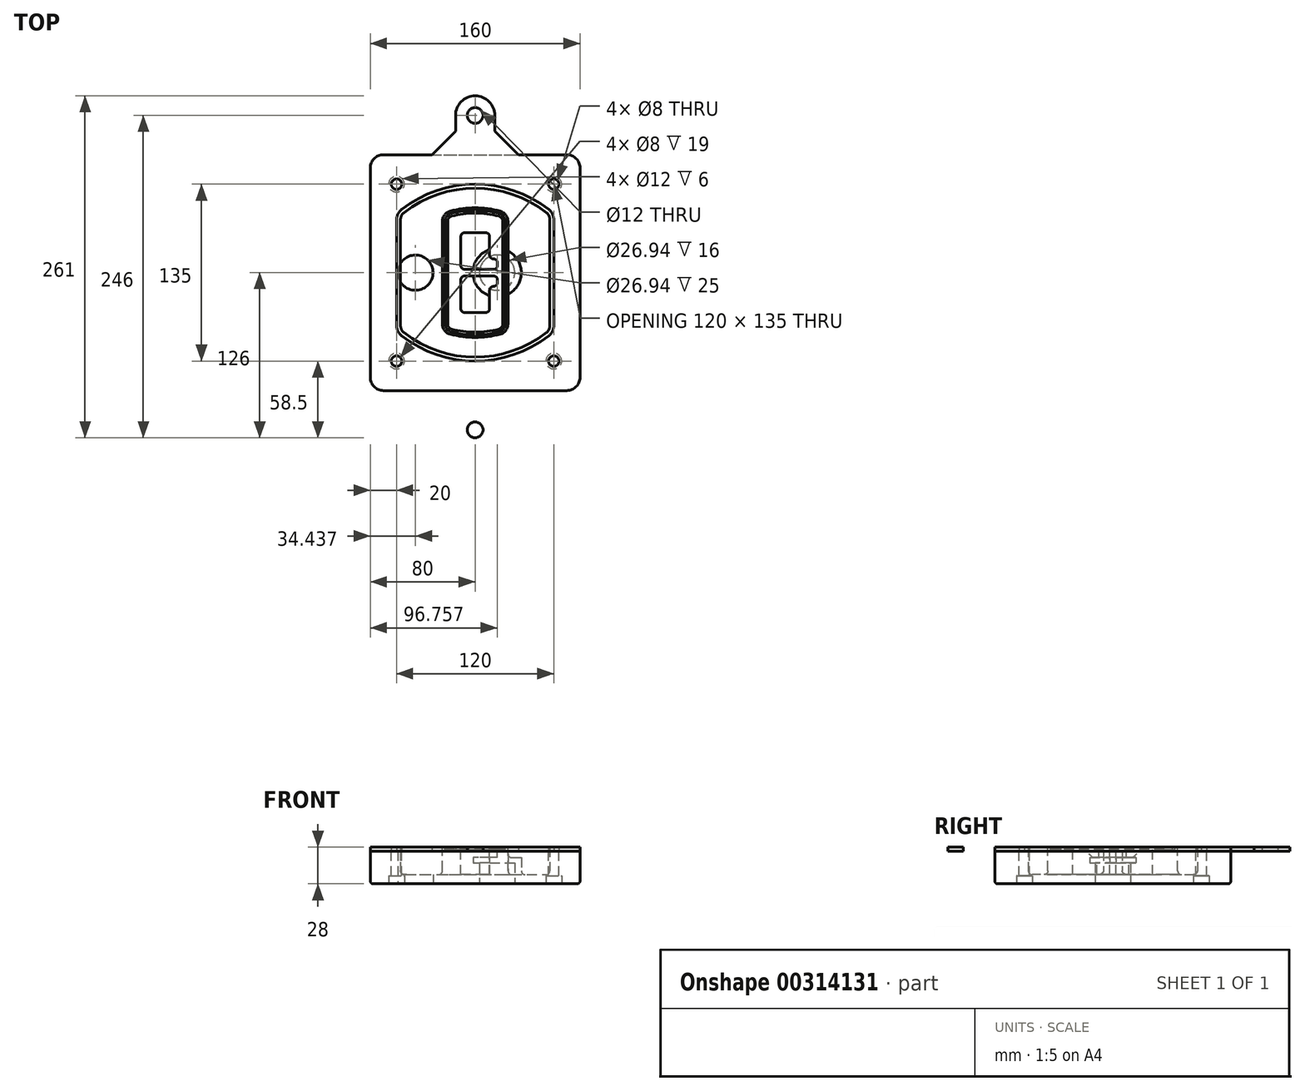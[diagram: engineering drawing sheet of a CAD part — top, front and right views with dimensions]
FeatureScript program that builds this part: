
annotation { "Feature Type Name" : "Feature", "Feature Type Description" : "" }
export const myFeature = defineFeature(function(context is Context, id is Id, definition is map)
    precondition{}
    {
        {
            var Q0;
            Q0=qCreatedBy(makeId("Top.planeOp"),FACE);
            var sketch = newSketch(context, id + "F0", { "sketchPlane" : qUnion([Q0])});
            skPoint(sketch, "E0.rect.middle", {"position": v(0, 0) * mm});
            skLineSegment(sketch, "E1.bottom", {"start": v(-70, -90) * mm, "end": v(70, -90) * mm});
            skLineSegment(sketch, "E1.top", {"start": v(-70, 90) * mm, "end": v(70, 90) * mm});
            skLineSegment(sketch, "E1.left", {"start": v(-80, -80) * mm, "end": v(-80, 80) * mm});
            skLineSegment(sketch, "E1.right", {"start": v(80, -80) * mm, "end": v(80, 80) * mm});
            skLineSegment(sketch, "E2", {"start": v(-80, 90) * mm, "end": v(80, -90) * mm, "construction": true});
            skLineSegment(sketch, "E3", {"start": v(80, 90) * mm, "end": v(-80, -90) * mm, "construction": true});
            skCircle(sketch, "E4", {"center": v(-60, 67.5) * mm, "radius": 4 * mm});
            skCircle(sketch, "E5", {"center": v(60, 67.5) * mm, "radius": 4 * mm});
            skCircle(sketch, "E6", {"center": v(60, -67.5) * mm, "radius": 4 * mm});
            skCircle(sketch, "E7", {"center": v(-60, -67.5) * mm, "radius": 4 * mm});
            skLineSegment(sketch, "E8", {"start": v(-60, 67.5) * mm, "end": v(60, 67.5) * mm, "construction": true});
            skLineSegment(sketch, "E9", {"start": v(60, 67.5) * mm, "end": v(60, -67.5) * mm, "construction": true});
            skLineSegment(sketch, "E10", {"start": v(60, -67.5) * mm, "end": v(-60, -67.5) * mm, "construction": true});
            skLineSegment(sketch, "E11", {"start": v(-60, -67.5) * mm, "end": v(-60, 67.5) * mm, "construction": true});
            skLineSegment(sketch, "E12", {"start": v(-60, 40.3) * mm, "end": v(-60, -40.3) * mm});
            skLineSegment(sketch, "E13", {"start": v(60, 40.3) * mm, "end": v(60, -40.3) * mm});
            skArc(sketch, "E14", {"start": v(56.15, 48.18) * mm, "mid": v(0, 67.5) * mm, "end": v(-56.15, 48.18) * mm});
            skArc(sketch, "E15", {"start": v(-56.15, -48.18) * mm, "mid": v(0, -67.5) * mm, "end": v(56.15, -48.18) * mm});
            skLineSegment(sketch, "E16", {"start": v(-60, 0) * mm, "end": v(60, 0) * mm, "construction": true});
            skPoint(sketch, "E17.visualSharp", {"position": v(-60, -45) * mm});
            skArc(sketch, "E17.filletArc", {"start": v(-60, -40.3) * mm, "mid": v(-58.99, -44.68) * mm, "end": v(-56.15, -48.18) * mm});
            skPoint(sketch, "E18.visualSharp", {"position": v(-60, 45) * mm});
            skArc(sketch, "E18.filletArc", {"start": v(-56.15, 48.18) * mm, "mid": v(-58.99, 44.68) * mm, "end": v(-60, 40.3) * mm});
            skPoint(sketch, "E19.visualSharp", {"position": v(60, 45) * mm});
            skArc(sketch, "E19.filletArc", {"start": v(60, 40.3) * mm, "mid": v(58.99, 44.68) * mm, "end": v(56.15, 48.18) * mm});
            skPoint(sketch, "E20.visualSharp", {"position": v(60, -45) * mm});
            skArc(sketch, "E20.filletArc", {"start": v(56.15, -48.18) * mm, "mid": v(58.99, -44.68) * mm, "end": v(60, -40.3) * mm});
            skPoint(sketch, "E21.visualSharp", {"position": v(-80, 90) * mm});
            skArc(sketch, "E21.filletArc", {"start": v(-70, 90) * mm, "mid": v(-77.07, 87.07) * mm, "end": v(-80, 80) * mm});
            skPoint(sketch, "E22.visualSharp", {"position": v(80, 90) * mm});
            skArc(sketch, "E22.filletArc", {"start": v(80, 80) * mm, "mid": v(77.07, 87.07) * mm, "end": v(70, 90) * mm});
            skPoint(sketch, "E23.visualSharp", {"position": v(80, -90) * mm});
            skArc(sketch, "E23.filletArc", {"start": v(70, -90) * mm, "mid": v(77.07, -87.07) * mm, "end": v(80, -80) * mm});
            skPoint(sketch, "E24.visualSharp", {"position": v(-80, -90) * mm});
            skArc(sketch, "E24.filletArc", {"start": v(-80, -80) * mm, "mid": v(-77.07, -87.07) * mm, "end": v(-70, -90) * mm});
            skArc(sketch, "E25.0", {"start": v(57, 40.3) * mm, "mid": v(56.3, 43.36) * mm, "end": v(54.3, 45.81) * mm});
            skLineSegment(sketch, "E25.1", {"start": v(57, 40.3) * mm, "end": v(57, -40.3) * mm});
            skArc(sketch, "E25.2", {"start": v(54.3, -45.81) * mm, "mid": v(56.3, -43.36) * mm, "end": v(57, -40.3) * mm});
            skArc(sketch, "E25.3", {"start": v(-54.3, -45.81) * mm, "mid": v(0, -64.5) * mm, "end": v(54.3, -45.81) * mm});
            skArc(sketch, "E25.4", {"start": v(-57, -40.3) * mm, "mid": v(-56.3, -43.36) * mm, "end": v(-54.3, -45.81) * mm});
            skArc(sketch, "E25.5", {"start": v(54.3, 45.81) * mm, "mid": v(0, 64.5) * mm, "end": v(-54.3, 45.81) * mm});
            skLineSegment(sketch, "E25.6", {"start": v(-57, 40.3) * mm, "end": v(-57, -40.3) * mm});
            skArc(sketch, "E25.7", {"start": v(-54.3, 45.81) * mm, "mid": v(-56.3, 43.36) * mm, "end": v(-57, 40.3) * mm});
            skArc(sketch, "E26.0", {"start": v(-58.62, 51.33) * mm, "mid": v(-62.58, 46.43) * mm, "end": v(-64, 40.3) * mm});
            skArc(sketch, "E26.1", {"start": v(58.62, 51.33) * mm, "mid": v(0, 71.5) * mm, "end": v(-58.62, 51.33) * mm});
            skArc(sketch, "E26.2", {"start": v(64, 40.3) * mm, "mid": v(62.58, 46.43) * mm, "end": v(58.62, 51.33) * mm});
            skLineSegment(sketch, "E26.3", {"start": v(64, 40.3) * mm, "end": v(64, -40.3) * mm});
            skArc(sketch, "E26.4", {"start": v(58.62, -51.33) * mm, "mid": v(62.58, -46.43) * mm, "end": v(64, -40.3) * mm});
            skLineSegment(sketch, "E26.5", {"start": v(-64, 40.3) * mm, "end": v(-64, -40.3) * mm});
            skArc(sketch, "E26.6", {"start": v(-58.62, -51.33) * mm, "mid": v(0, -71.5) * mm, "end": v(58.62, -51.33) * mm});
            skArc(sketch, "E26.7", {"start": v(-64, -40.3) * mm, "mid": v(-62.58, -46.43) * mm, "end": v(-58.62, -51.33) * mm});
            skSolve(sketch);
        }
        {
            var Q0;
            Q0=makeQuery(id+"F0.imprint","IMPRINT",FACE,{"disambiguationData":[TD([[makeQuery(id+"F0.imprint","IMPRINT",EDGE,{"derivedFrom":sQuery(id+"F0.wireOp",EDGE,"E1.bottom")}),1.0]])]});
            var Q1;
            Q1=makeQuery(id+"F0.imprint","IMPRINT",FACE,{"disambiguationData":[TD([[makeQuery(id+"F0.imprint","IMPRINT",EDGE,{"derivedFrom":sQuery(id+"F0.wireOp",EDGE,"E12")}),1.0]])]});
            var Q2;
            Q2=makeQuery(id+"F0.imprint","IMPRINT",FACE,{"disambiguationData":[TD([[makeQuery(id+"F0.imprint","IMPRINT",EDGE,{"derivedFrom":sQuery(id+"F0.wireOp",EDGE,"E25.0")}),1.0]])]});
            var Q3;
            Q3=makeQuery(id+"F0.imprint","IMPRINT",FACE,{"disambiguationData":[TD([[makeQuery(id+"F0.imprint","IMPRINT",EDGE,{"derivedFrom":sQuery(id+"F0.wireOp",EDGE,"E12")}),-1.0]])]});
            extrude(context, id + "F1", {"entities" : qUnion([Q0, Q1, Q2, Q3]), "oppositeDirection" : true, "depth" : 25 * mm});
        }
        {
            var Q0;
            Q0=makeQuery(id+"F0.imprint","IMPRINT",FACE,{"disambiguationData":[TD([[makeQuery(id+"F0.imprint","IMPRINT",EDGE,{"derivedFrom":sQuery(id+"F0.wireOp",EDGE,"E12")}),1.0]])]});
            extrude(context, id + "F2", {"entities" : qUnion([Q0]), "operationType" : NewBodyOperationType.ADD, "depth" : 3 * mm});
        }
        {
            var Q0;
            Q0=makeQuery(id+"F0.imprint","IMPRINT",FACE,{"disambiguationData":[TD([[makeQuery(id+"F0.imprint","IMPRINT",EDGE,{"derivedFrom":sQuery(id+"F0.wireOp",EDGE,"E25.0")}),1.0]])]});
            extrude(context, id + "F3", {"entities" : qUnion([Q0]), "operationType" : NewBodyOperationType.REMOVE, "oppositeDirection" : true, "depth" : 18 * mm});
        }
        {
            var Q0;
            Q0=makeQuery(id+"F2.opExtrude","CAP_FACE",FACE,{"disambiguationData":[OSD([sQuery(id+"F0.wireOp",EDGE,"E12"),sQuery(id+"F0.wireOp",EDGE,"E13"),sQuery(id+"F0.wireOp",EDGE,"E14"),sQuery(id+"F0.wireOp",EDGE,"E15"),sQuery(id+"F0.wireOp",EDGE,"E17.filletArc"),sQuery(id+"F0.wireOp",EDGE,"E18.filletArc"),sQuery(id+"F0.wireOp",EDGE,"E19.filletArc"),sQuery(id+"F0.wireOp",EDGE,"E20.filletArc"),sQuery(id+"F0.wireOp",EDGE,"E25.0"),sQuery(id+"F0.wireOp",EDGE,"E25.1"),sQuery(id+"F0.wireOp",EDGE,"E25.2"),sQuery(id+"F0.wireOp",EDGE,"E25.3"),sQuery(id+"F0.wireOp",EDGE,"E25.4"),sQuery(id+"F0.wireOp",EDGE,"E25.5"),sQuery(id+"F0.wireOp",EDGE,"E25.6"),sQuery(id+"F0.wireOp",EDGE,"E25.7")])],"isStart":false});
            var sketch = newSketch(context, id + "F4", { "sketchPlane" : qUnion([Q0])});
            skArc(sketch, "E27.0", {"start": v(-19.08, -46.97) * mm, "mid": v(0, -49.5) * mm, "end": v(19.08, -46.97) * mm});
            skArc(sketch, "E28.0", {"start": v(19.08, 46.97) * mm, "mid": v(0, 49.5) * mm, "end": v(-19.08, 46.97) * mm});
            skLineSegment(sketch, "E29", {"start": v(-25, 39.25) * mm, "end": v(-25, -39.25) * mm});
            skLineSegment(sketch, "E30", {"start": v(25, 39.25) * mm, "end": v(25, -39.25) * mm});
            skLineSegment(sketch, "E31", {"start": v(-25, 45.1) * mm, "end": v(25, 45.1) * mm, "construction": true});
            skLineSegment(sketch, "E32", {"start": v(-25, -45.1) * mm, "end": v(25, -45.1) * mm, "construction": true});
            skPoint(sketch, "E33.visualSharp", {"position": v(-25, 45.1) * mm});
            skArc(sketch, "E33.filletArc", {"start": v(-19.08, 46.97) * mm, "mid": v(-23.35, 44.11) * mm, "end": v(-25, 39.25) * mm});
            skPoint(sketch, "E34.visualSharp", {"position": v(25, 45.1) * mm});
            skArc(sketch, "E34.filletArc", {"start": v(25, 39.25) * mm, "mid": v(23.35, 44.11) * mm, "end": v(19.08, 46.97) * mm});
            skPoint(sketch, "E35.visualSharp", {"position": v(25, -45.1) * mm});
            skArc(sketch, "E35.filletArc", {"start": v(19.08, -46.97) * mm, "mid": v(23.35, -44.11) * mm, "end": v(25, -39.25) * mm});
            skPoint(sketch, "E36.visualSharp", {"position": v(-25, -45.1) * mm});
            skArc(sketch, "E36.filletArc", {"start": v(-25, -39.25) * mm, "mid": v(-23.35, -44.11) * mm, "end": v(-19.08, -46.97) * mm});
            skArc(sketch, "E37.0", {"start": v(54.3, 45.81) * mm, "mid": v(0, 64.5) * mm, "end": v(-54.3, 45.81) * mm});
            skArc(sketch, "E37.1", {"start": v(-54.3, 45.81) * mm, "mid": v(-56.3, 43.36) * mm, "end": v(-57, 40.3) * mm});
            skLineSegment(sketch, "E37.2", {"start": v(-57, 40.3) * mm, "end": v(-57, -40.3) * mm});
            skArc(sketch, "E37.3", {"start": v(-57, -40.3) * mm, "mid": v(-56.3, -43.36) * mm, "end": v(-54.3, -45.81) * mm});
            skArc(sketch, "E37.4", {"start": v(-54.3, -45.81) * mm, "mid": v(0, -64.5) * mm, "end": v(54.3, -45.81) * mm});
            skArc(sketch, "E37.5", {"start": v(54.3, -45.81) * mm, "mid": v(56.3, -43.36) * mm, "end": v(57, -40.3) * mm});
            skLineSegment(sketch, "E37.6", {"start": v(57, 40.3) * mm, "end": v(57, -40.3) * mm});
            skArc(sketch, "E37.7", {"start": v(57, 40.3) * mm, "mid": v(56.3, 43.36) * mm, "end": v(54.3, 45.81) * mm});
            skLineSegment(sketch, "E38.0", {"start": v(23, 39.25) * mm, "end": v(23, -39.25) * mm});
            skArc(sketch, "E38.1", {"start": v(18.56, -45.04) * mm, "mid": v(21.76, -42.9) * mm, "end": v(23, -39.25) * mm});
            skArc(sketch, "E38.2", {"start": v(-18.56, -45.04) * mm, "mid": v(0, -47.5) * mm, "end": v(18.56, -45.04) * mm});
            skArc(sketch, "E38.3", {"start": v(-23, -39.25) * mm, "mid": v(-21.76, -42.9) * mm, "end": v(-18.56, -45.04) * mm});
            skLineSegment(sketch, "E38.4", {"start": v(-23, 39.25) * mm, "end": v(-23, -39.25) * mm});
            skArc(sketch, "E38.5", {"start": v(23, 39.25) * mm, "mid": v(21.76, 42.9) * mm, "end": v(18.56, 45.04) * mm});
            skArc(sketch, "E38.6", {"start": v(-18.56, 45.04) * mm, "mid": v(-21.76, 42.9) * mm, "end": v(-23, 39.25) * mm});
            skArc(sketch, "E38.7", {"start": v(18.56, 45.04) * mm, "mid": v(0, 47.5) * mm, "end": v(-18.56, 45.04) * mm});
            skArc(sketch, "E39.0", {"start": v(21, 39.25) * mm, "mid": v(20.18, 41.68) * mm, "end": v(18.04, 43.1) * mm});
            skLineSegment(sketch, "E39.1", {"start": v(21, 39.25) * mm, "end": v(21, -39.25) * mm});
            skArc(sketch, "E39.2", {"start": v(18.04, -43.1) * mm, "mid": v(20.18, -41.68) * mm, "end": v(21, -39.25) * mm});
            skArc(sketch, "E39.3", {"start": v(-18.04, -43.1) * mm, "mid": v(0, -45.5) * mm, "end": v(18.04, -43.1) * mm});
            skArc(sketch, "E39.4", {"start": v(-21, -39.25) * mm, "mid": v(-20.18, -41.68) * mm, "end": v(-18.04, -43.1) * mm});
            skArc(sketch, "E39.5", {"start": v(18.04, 43.1) * mm, "mid": v(0, 45.5) * mm, "end": v(-18.04, 43.1) * mm});
            skLineSegment(sketch, "E39.6", {"start": v(-21, 39.25) * mm, "end": v(-21, -39.25) * mm});
            skArc(sketch, "E39.7", {"start": v(-18.04, 43.1) * mm, "mid": v(-20.18, 41.68) * mm, "end": v(-21, 39.25) * mm});
            skLineSegment(sketch, "E40", {"start": v(-25, 0) * mm, "end": v(25, 0) * mm, "construction": true});
            skLineSegment(sketch, "E41", {"start": v(-11, 5.5) * mm, "end": v(-11, 27.5) * mm});
            skLineSegment(sketch, "E42", {"start": v(-8, 30.5) * mm, "end": v(8, 30.5) * mm});
            skLineSegment(sketch, "E43", {"start": v(11, 27.5) * mm, "end": v(11, 13.5) * mm});
            skLineSegment(sketch, "E44", {"start": v(14, 10.5) * mm, "end": v(14, 10.5) * mm});
            skLineSegment(sketch, "E45", {"start": v(17, 7.5) * mm, "end": v(17, 5.5) * mm});
            skLineSegment(sketch, "E46", {"start": v(14, 2.5) * mm, "end": v(-8, 2.5) * mm});
            skPoint(sketch, "E47.visualSharp", {"position": v(-11, 30.5) * mm});
            skArc(sketch, "E47.filletArc", {"start": v(-8, 30.5) * mm, "mid": v(-10.12, 29.62) * mm, "end": v(-11, 27.5) * mm});
            skPoint(sketch, "E48.visualSharp", {"position": v(11, 30.5) * mm});
            skArc(sketch, "E48.filletArc", {"start": v(11, 27.5) * mm, "mid": v(10.12, 29.62) * mm, "end": v(8, 30.5) * mm});
            skPoint(sketch, "E49.visualSharp", {"position": v(11, 10.5) * mm});
            skArc(sketch, "E49.filletArc", {"start": v(11, 13.5) * mm, "mid": v(11.88, 11.38) * mm, "end": v(14, 10.5) * mm});
            skPoint(sketch, "E50.visualSharp", {"position": v(17, 10.5) * mm});
            skArc(sketch, "E50.filletArc", {"start": v(17, 7.5) * mm, "mid": v(16.12, 9.62) * mm, "end": v(14, 10.5) * mm});
            skPoint(sketch, "E51.visualSharp", {"position": v(17, 2.5) * mm});
            skArc(sketch, "E51.filletArc", {"start": v(14, 2.5) * mm, "mid": v(16.12, 3.38) * mm, "end": v(17, 5.5) * mm});
            skPoint(sketch, "E52.visualSharp", {"position": v(-11, 2.5) * mm});
            skArc(sketch, "E52.filletArc", {"start": v(-11, 5.5) * mm, "mid": v(-10.12, 3.38) * mm, "end": v(-8, 2.5) * mm});
            skLineSegment(sketch, "E53.0.MirrorCS", {"start": v(14, -2.5) * mm, "end": v(-8, -2.5) * mm});
            skArc(sketch, "E54.0.MirrorCS", {"start": v(-11, -5.5) * mm, "mid": v(-10.12, -3.38) * mm, "end": v(-8, -2.5) * mm});
            skLineSegment(sketch, "E55.0.MirrorCS", {"start": v(-11, -5.5) * mm, "end": v(-11, -27.5) * mm});
            skArc(sketch, "E56.0.MirrorCS", {"start": v(-8, -30.5) * mm, "mid": v(-10.12, -29.62) * mm, "end": v(-11, -27.5) * mm});
            skLineSegment(sketch, "E57.0.MirrorCS", {"start": v(-8, -30.5) * mm, "end": v(8, -30.5) * mm});
            skArc(sketch, "E58.0.MirrorCS", {"start": v(11, -27.5) * mm, "mid": v(10.12, -29.62) * mm, "end": v(8, -30.5) * mm});
            skLineSegment(sketch, "E59.0.MirrorCS", {"start": v(11, -27.5) * mm, "end": v(11, -13.5) * mm});
            skArc(sketch, "E60.0.MirrorCS", {"start": v(11, -13.5) * mm, "mid": v(11.88, -11.38) * mm, "end": v(14, -10.5) * mm});
            skArc(sketch, "E61.0.MirrorCS", {"start": v(17, -7.5) * mm, "mid": v(16.12, -9.62) * mm, "end": v(14, -10.5) * mm});
            skLineSegment(sketch, "E62.0.MirrorCS", {"start": v(17, -7.5) * mm, "end": v(17, -5.5) * mm});
            skArc(sketch, "E63.0.MirrorCS", {"start": v(14, -2.5) * mm, "mid": v(16.12, -3.38) * mm, "end": v(17, -5.5) * mm});
            skSolve(sketch);
        }
        {
            var Q0;
            Q0=makeQuery(id+"F4.imprint","IMPRINT",FACE,{"disambiguationData":[TD([[makeQuery(id+"F4.imprint","IMPRINT",EDGE,{"derivedFrom":sQuery(id+"F4.wireOp",EDGE,"E27.0")}),1.0]])]});
            var Q1;
            Q1=makeQuery(id+"F4.imprint","IMPRINT",FACE,{"disambiguationData":[TD([[makeQuery(id+"F4.imprint","IMPRINT",EDGE,{"derivedFrom":sQuery(id+"F4.wireOp",EDGE,"E38.0")}),-1.0]])]});
            var Q2;
            Q2=makeQuery(id+"F4.imprint","IMPRINT",FACE,{"disambiguationData":[TD([[makeQuery(id+"F4.imprint","IMPRINT",EDGE,{"derivedFrom":sQuery(id+"F4.wireOp",EDGE,"E39.0")}),1.0]])]});
            extrude(context, id + "F5", {"entities" : qUnion([Q0, Q1, Q2]), "operationType" : NewBodyOperationType.ADD, "endBound" : BoundingType.UP_TO_NEXT, "oppositeDirection" : true, "depth" : 25 * mm});
        }
        {
            var Q0;
            Q0=makeQuery(id+"F4.imprint","IMPRINT",FACE,{"disambiguationData":[TD([[makeQuery(id+"F4.imprint","IMPRINT",EDGE,{"derivedFrom":sQuery(id+"F4.wireOp",EDGE,"E38.0")}),-1.0]])]});
            extrude(context, id + "F6", {"entities" : qUnion([Q0]), "operationType" : NewBodyOperationType.REMOVE, "oppositeDirection" : true, "depth" : 2 * mm});
        }
        {
            var Q0;
            Q0=makeQuery(id+"F1.opExtrude","CAP_FACE",FACE,{"disambiguationData":[OSD([sQuery(id+"F0.wireOp",EDGE,"E1.bottom"),sQuery(id+"F0.wireOp",EDGE,"E1.top"),sQuery(id+"F0.wireOp",EDGE,"E1.left"),sQuery(id+"F0.wireOp",EDGE,"E1.right"),sQuery(id+"F0.wireOp",EDGE,"E4"),sQuery(id+"F0.wireOp",EDGE,"E5"),sQuery(id+"F0.wireOp",EDGE,"E6"),sQuery(id+"F0.wireOp",EDGE,"E7"),sQuery(id+"F0.wireOp",EDGE,"E21.filletArc"),sQuery(id+"F0.wireOp",EDGE,"E22.filletArc"),sQuery(id+"F0.wireOp",EDGE,"E23.filletArc"),sQuery(id+"F0.wireOp",EDGE,"E24.filletArc")])],"isStart":false});
            var sketch = newSketch(context, id + "F7", { "sketchPlane" : qUnion([Q0])});
            skCircle(sketch, "E64", {"center": v(16.76, 0) * mm, "radius": 13.47 * mm});
            skCircle(sketch, "E65", {"center": v(-45.56, 0) * mm, "radius": 13.47 * mm});
            skLineSegment(sketch, "E66", {"start": v(80, 0) * mm, "end": v(-80, 0) * mm});
            skCircle(sketch, "E67", {"center": v(16.76, 0) * mm, "radius": 18.47 * mm});
            skCircle(sketch, "E68", {"center": v(60, -67.5) * mm, "radius": 6 * mm});
            skCircle(sketch, "E69", {"center": v(-60, -67.5) * mm, "radius": 6 * mm});
            skCircle(sketch, "E70", {"center": v(-60, 67.5) * mm, "radius": 6 * mm});
            skCircle(sketch, "E71", {"center": v(60, 67.5) * mm, "radius": 6 * mm});
            skSolve(sketch);
        }
        {
            var Q0;
            {var subQ1=sQuery(id+"F7.wireOp",EDGE,"E66");var subQ4=sQuery(id+"F7.wireOp",EDGE,"E64");var subQ6=makeQuery(id+"F7.imprint","INTERSECT",VERTEX,{"disambiguationData":[OD(0.0)],"derivedFrom":[subQ4,subQ1]});Q0=makeQuery(id+"F7.imprint","IMPRINT",FACE,{"disambiguationData":[TD([[makeQuery(id+"F7.imprint","IMPRINT",EDGE,{"disambiguationData":[TD([[subQ6,-1.0]])],"derivedFrom":subQ4}),-1.0]])]});}
            var Q1;
            {var subQ0=sQuery(id+"F7.wireOp",EDGE,"E66");var subQ1=sQuery(id+"F7.wireOp",EDGE,"E64");var subQ3=makeQuery(id+"F7.imprint","INTERSECT",VERTEX,{"disambiguationData":[OD(0.0)],"derivedFrom":[subQ1,subQ0]});Q1=makeQuery(id+"F7.imprint","IMPRINT",FACE,{"disambiguationData":[TD([[makeQuery(id+"F7.imprint","IMPRINT",EDGE,{"disambiguationData":[TD([[subQ3,-1.0]])],"derivedFrom":subQ1}),1.0]])]});}
            var Q2;
            {var subQ0=sQuery(id+"F7.wireOp",EDGE,"E66");var subQ1=sQuery(id+"F7.wireOp",EDGE,"E64");var subQ3=makeQuery(id+"F7.imprint","INTERSECT",VERTEX,{"disambiguationData":[OD(0.0)],"derivedFrom":[subQ1,subQ0]});Q2=makeQuery(id+"F7.imprint","IMPRINT",FACE,{"disambiguationData":[TD([[makeQuery(id+"F7.imprint","IMPRINT",EDGE,{"disambiguationData":[TD([[subQ3,1.0]])],"derivedFrom":subQ1}),1.0]])]});}
            var Q3;
            {var subQ1=sQuery(id+"F7.wireOp",EDGE,"E66");var subQ4=sQuery(id+"F7.wireOp",EDGE,"E64");var subQ6=makeQuery(id+"F7.imprint","INTERSECT",VERTEX,{"disambiguationData":[OD(0.0)],"derivedFrom":[subQ4,subQ1]});Q3=makeQuery(id+"F7.imprint","IMPRINT",FACE,{"disambiguationData":[TD([[makeQuery(id+"F7.imprint","IMPRINT",EDGE,{"disambiguationData":[TD([[subQ6,1.0]])],"derivedFrom":subQ4}),-1.0]])]});}
            extrude(context, id + "F8", {"entities" : qUnion([Q0, Q1, Q2, Q3]), "operationType" : NewBodyOperationType.ADD, "oppositeDirection" : true, "depth" : 20 * mm});
        }
        {
            var Q0;
            {var subQ0=sQuery(id+"F7.wireOp",EDGE,"E66");var subQ1=sQuery(id+"F7.wireOp",EDGE,"E64");var subQ3=makeQuery(id+"F7.imprint","INTERSECT",VERTEX,{"disambiguationData":[OD(0.0)],"derivedFrom":[subQ1,subQ0]});Q0=makeQuery(id+"F7.imprint","IMPRINT",FACE,{"disambiguationData":[TD([[makeQuery(id+"F7.imprint","IMPRINT",EDGE,{"disambiguationData":[TD([[subQ3,-1.0]])],"derivedFrom":subQ1}),1.0]])]});}
            var Q1;
            {var subQ0=sQuery(id+"F7.wireOp",EDGE,"E66");var subQ1=sQuery(id+"F7.wireOp",EDGE,"E64");var subQ3=makeQuery(id+"F7.imprint","INTERSECT",VERTEX,{"disambiguationData":[OD(0.0)],"derivedFrom":[subQ1,subQ0]});Q1=makeQuery(id+"F7.imprint","IMPRINT",FACE,{"disambiguationData":[TD([[makeQuery(id+"F7.imprint","IMPRINT",EDGE,{"disambiguationData":[TD([[subQ3,1.0]])],"derivedFrom":subQ1}),1.0]])]});}
            extrude(context, id + "F9", {"entities" : qUnion([Q0, Q1]), "operationType" : NewBodyOperationType.REMOVE, "oppositeDirection" : true, "depth" : 16 * mm});
        }
        {
            var Q0;
            {var subQ0=sQuery(id+"F7.wireOp",EDGE,"E66");var subQ1=sQuery(id+"F7.wireOp",EDGE,"E65");var subQ3=makeQuery(id+"F7.imprint","INTERSECT",VERTEX,{"disambiguationData":[OD(0.0)],"derivedFrom":[subQ1,subQ0]});Q0=makeQuery(id+"F7.imprint","IMPRINT",FACE,{"disambiguationData":[TD([[makeQuery(id+"F7.imprint","IMPRINT",EDGE,{"disambiguationData":[TD([[subQ3,-1.0]])],"derivedFrom":subQ1}),1.0]])]});}
            var Q1;
            {var subQ0=sQuery(id+"F7.wireOp",EDGE,"E66");var subQ1=sQuery(id+"F7.wireOp",EDGE,"E65");var subQ3=makeQuery(id+"F7.imprint","INTERSECT",VERTEX,{"disambiguationData":[OD(0.0)],"derivedFrom":[subQ1,subQ0]});Q1=makeQuery(id+"F7.imprint","IMPRINT",FACE,{"disambiguationData":[TD([[makeQuery(id+"F7.imprint","IMPRINT",EDGE,{"disambiguationData":[TD([[subQ3,1.0]])],"derivedFrom":subQ1}),1.0]])]});}
            extrude(context, id + "F10", {"entities" : qUnion([Q0, Q1]), "operationType" : NewBodyOperationType.REMOVE, "oppositeDirection" : true, "depth" : 25 * mm});
        }
        {
            var Q0;
            Q0=makeQuery(id+"F7.imprint","IMPRINT",FACE,{"disambiguationData":[TD([[makeQuery(id+"F7.imprint","IMPRINT",EDGE,{"derivedFrom":sQuery(id+"F7.wireOp",EDGE,"E68")}),1.0]])]});
            var Q1;
            Q1=makeQuery(id+"F7.imprint","IMPRINT",FACE,{"disambiguationData":[TD([[makeQuery(id+"F7.imprint","IMPRINT",EDGE,{"derivedFrom":makeQuery(id+"F1.opExtrude","CAP_EDGE",EDGE,{"disambiguationData":[OSD([sQuery(id+"F0.wireOp",EDGE,"E5")])],"isStart":false})}),-1.0]])]});
            var Q2;
            Q2=makeQuery(id+"F7.imprint","IMPRINT",FACE,{"disambiguationData":[TD([[makeQuery(id+"F7.imprint","IMPRINT",EDGE,{"derivedFrom":sQuery(id+"F7.wireOp",EDGE,"E69")}),1.0]])]});
            var Q3;
            Q3=makeQuery(id+"F7.imprint","IMPRINT",FACE,{"disambiguationData":[TD([[makeQuery(id+"F7.imprint","IMPRINT",EDGE,{"derivedFrom":makeQuery(id+"F1.opExtrude","CAP_EDGE",EDGE,{"disambiguationData":[OSD([sQuery(id+"F0.wireOp",EDGE,"E4")])],"isStart":false})}),-1.0]])]});
            var Q4;
            Q4=makeQuery(id+"F7.imprint","IMPRINT",FACE,{"disambiguationData":[TD([[makeQuery(id+"F7.imprint","IMPRINT",EDGE,{"derivedFrom":sQuery(id+"F7.wireOp",EDGE,"E70")}),1.0]])]});
            var Q5;
            Q5=makeQuery(id+"F7.imprint","IMPRINT",FACE,{"disambiguationData":[TD([[makeQuery(id+"F7.imprint","IMPRINT",EDGE,{"derivedFrom":makeQuery(id+"F1.opExtrude","CAP_EDGE",EDGE,{"disambiguationData":[OSD([sQuery(id+"F0.wireOp",EDGE,"E7")])],"isStart":false})}),-1.0]])]});
            var Q6;
            Q6=makeQuery(id+"F7.imprint","IMPRINT",FACE,{"disambiguationData":[TD([[makeQuery(id+"F7.imprint","IMPRINT",EDGE,{"derivedFrom":sQuery(id+"F7.wireOp",EDGE,"E71")}),1.0]])]});
            var Q7;
            Q7=makeQuery(id+"F7.imprint","IMPRINT",FACE,{"disambiguationData":[TD([[makeQuery(id+"F7.imprint","IMPRINT",EDGE,{"derivedFrom":makeQuery(id+"F1.opExtrude","CAP_EDGE",EDGE,{"disambiguationData":[OSD([sQuery(id+"F0.wireOp",EDGE,"E6")])],"isStart":false})}),-1.0]])]});
            extrude(context, id + "F11", {"entities" : qUnion([Q0, Q1, Q2, Q3, Q4, Q5, Q6, Q7]), "operationType" : NewBodyOperationType.REMOVE, "oppositeDirection" : true, "depth" : 6 * mm});
        }
        {
            var Q0;
            Q0=makeQuery(id+"F9.boolean.opBoolean","COPY",FACE,{"derivedFrom":makeQuery(id+"F9.opExtrude","CAP_FACE",FACE,{"disambiguationData":[OSD([sQuery(id+"F7.wireOp",EDGE,"E64")])],"isStart":false})});
            var sketch = newSketch(context, id + "F12", { "sketchPlane" : qUnion([Q0])});
            skArc(sketch, "E72.0", {"start": v(11, 17.55) * mm, "mid": v(2.57, 11.82) * mm, "end": v(-1.54, 2.5) * mm});
            skArc(sketch, "E72.1", {"start": v(-1.54, -2.5) * mm, "mid": v(2.57, -11.82) * mm, "end": v(11, -17.55) * mm});
            skLineSegment(sketch, "E73", {"start": v(-1.54, -2.5) * mm, "end": v(14, -2.5) * mm});
            skLineSegment(sketch, "E74.0", {"start": v(14, 2.5) * mm, "end": v(-1.54, 2.5) * mm});
            skArc(sketch, "E74.1", {"start": v(14, 2.5) * mm, "mid": v(16.12, 3.38) * mm, "end": v(17, 5.5) * mm});
            skLineSegment(sketch, "E74.2", {"start": v(17, 7.5) * mm, "end": v(17, 5.5) * mm});
            skArc(sketch, "E74.3", {"start": v(17, 7.5) * mm, "mid": v(16.12, 9.62) * mm, "end": v(14, 10.5) * mm});
            skArc(sketch, "E74.4", {"start": v(11, 13.5) * mm, "mid": v(11.88, 11.38) * mm, "end": v(14, 10.5) * mm});
            skLineSegment(sketch, "E74.5", {"start": v(11, 17.55) * mm, "end": v(11, 13.5) * mm});
            skLineSegment(sketch, "E74.7", {"start": v(14, -2.5) * mm, "end": v(-1.54, -2.5) * mm});
            skArc(sketch, "E74.8", {"start": v(14, -2.5) * mm, "mid": v(16.12, -3.38) * mm, "end": v(17, -5.5) * mm});
            skLineSegment(sketch, "E74.9", {"start": v(17, -7.5) * mm, "end": v(17, -5.5) * mm});
            skArc(sketch, "E74.10", {"start": v(17, -7.5) * mm, "mid": v(16.12, -9.62) * mm, "end": v(14, -10.5) * mm});
            skArc(sketch, "E74.11", {"start": v(11, -13.5) * mm, "mid": v(11.88, -11.38) * mm, "end": v(14, -10.5) * mm});
            skLineSegment(sketch, "E74.12", {"start": v(11, -17.55) * mm, "end": v(11, -13.5) * mm});
            skPoint(sketch, "E75.orphan", {"position": v(11, -27.5) * mm});
            skPoint(sketch, "E76.orphan", {"position": v(-8, -2.5) * mm});
            skPoint(sketch, "E77.orphan", {"position": v(-8, 2.5) * mm});
            skPoint(sketch, "E78.orphan", {"position": v(11, 27.5) * mm});
            skSolve(sketch);
        }
        {
            var Q0;
            {var subQ7=sQuery(id+"F12.wireOp",EDGE,"E72.0");var subQ14=sQuery(id+"F12.wireOp",EDGE,"E72.1");var subQ16=sQuery(id+"F12.wireOp",EDGE,"E74.1");var subQ18=sQuery(id+"F12.wireOp",EDGE,"E74.8");Q0=qUnion([makeQuery(id+"F12.imprint","IMPRINT",FACE,{"disambiguationData":[TD([[makeQuery(id+"F12.imprint","IMPRINT",EDGE,{"derivedFrom":subQ7}),1.0]])]}),makeQuery(id+"F12.imprint","IMPRINT",FACE,{"disambiguationData":[TD([[makeQuery(id+"F12.imprint","IMPRINT",EDGE,{"derivedFrom":subQ14}),1.0]])]}),makeQuery(id+"F12.imprint","IMPRINT",FACE,{"disambiguationData":[TD([[makeQuery(id+"F12.imprint","IMPRINT",EDGE,{"derivedFrom":subQ16}),1.0]])]}),makeQuery(id+"F12.imprint","IMPRINT",FACE,{"disambiguationData":[TD([[makeQuery(id+"F12.imprint","IMPRINT",EDGE,{"derivedFrom":subQ18}),-1.0]])]})]);}
            var Q1;
            Q1=makeQuery(id+"F5.boolean.opBoolean","SPLIT",FACE,{"disambiguationData":[TD([makeQuery(id+"F5.opExtrude","SWEPT_FACE",FACE,{"disambiguationData":[OSD([sQuery(id+"F4.wireOp",EDGE,"E41")])]})])],"derivedFrom":makeQuery(id+"F3.boolean.opBoolean","COPY",FACE,{"derivedFrom":makeQuery(id+"F3.opExtrude","CAP_FACE",FACE,{"disambiguationData":[OSD([sQuery(id+"F0.wireOp",EDGE,"E25.0"),sQuery(id+"F0.wireOp",EDGE,"E25.1"),sQuery(id+"F0.wireOp",EDGE,"E25.2"),sQuery(id+"F0.wireOp",EDGE,"E25.3"),sQuery(id+"F0.wireOp",EDGE,"E25.4"),sQuery(id+"F0.wireOp",EDGE,"E25.5"),sQuery(id+"F0.wireOp",EDGE,"E25.6"),sQuery(id+"F0.wireOp",EDGE,"E25.7")])],"isStart":false})})});
            extrude(context, id + "F13", {"entities" : qUnion([Q0]), "operationType" : NewBodyOperationType.REMOVE, "endBound" : BoundingType.UP_TO_SURFACE, "endBoundEntityFace" : qUnion([Q1]), "depth" : 25 * mm});
        }
        {
            var Q0;
            Q0=makeQuery(id+"F3.boolean.opBoolean","COPY",EDGE,{"derivedFrom":makeQuery(id+"F3.opExtrude","CAP_EDGE",EDGE,{"disambiguationData":[OSD([sQuery(id+"F0.wireOp",EDGE,"E25.6")])],"isStart":false})});
            var Q1;
            Q1=makeQuery(id+"F8.boolean.opBoolean","INTERSECT",EDGE,{"derivedFrom":[makeQuery(id+"F5.opExtrude","SWEPT_FACE",FACE,{"disambiguationData":[OSD([sQuery(id+"F4.wireOp",EDGE,"E30")])]}),makeQuery(id+"F8.opExtrude","CAP_FACE",FACE,{"disambiguationData":[OSD([sQuery(id+"F7.wireOp",EDGE,"E67")])],"isStart":false})]});
            var Q2;
            Q2=makeQuery(id+"F8.boolean.opBoolean","INTERSECT",EDGE,{"disambiguationData":[OD(1.0)],"derivedFrom":[makeQuery(id+"F5.opExtrude","SWEPT_FACE",FACE,{"disambiguationData":[OSD([sQuery(id+"F4.wireOp",EDGE,"E30")])]}),makeQuery(id+"F8.opExtrude","SWEPT_FACE",FACE,{"disambiguationData":[OSD([sQuery(id+"F7.wireOp",EDGE,"E67")])]})]});
            var Q3;
            {var subQ0=sQuery(id+"F4.wireOp",EDGE,"E30");Q3=makeQuery(id+"F8.boolean.opBoolean","SPLIT",EDGE,{"disambiguationData":[TD([makeQuery(id+"F5.opExtrude","SWEPT_FACE",FACE,{"disambiguationData":[OSD([sQuery(id+"F4.wireOp",EDGE,"E35.filletArc")])]})])],"derivedFrom":makeQuery(id+"F5.opExtrude","CAP_EDGE",EDGE,{"disambiguationData":[OSD([subQ0])],"isStart":false})});}
            var Q4;
            {var subQ0=sQuery(id+"F0.wireOp",EDGE,"E25.7");var subQ1=sQuery(id+"F0.wireOp",EDGE,"E25.1");var subQ2=sQuery(id+"F0.wireOp",EDGE,"E25.6");var subQ3=sQuery(id+"F0.wireOp",EDGE,"E25.5");var subQ4=sQuery(id+"F0.wireOp",EDGE,"E25.4");var subQ5=sQuery(id+"F0.wireOp",EDGE,"E25.0");var subQ6=sQuery(id+"F0.wireOp",EDGE,"E25.2");var subQ7=sQuery(id+"F0.wireOp",EDGE,"E25.3");Q4=makeQuery(id+"F8.boolean.opBoolean","INTERSECT",EDGE,{"derivedFrom":[makeQuery(id+"F5.boolean.opBoolean","SPLIT",FACE,{"disambiguationData":[TD([makeQuery(id+"F2.opExtrude","SWEPT_FACE",FACE,{"disambiguationData":[OSD([subQ5])]})])],"derivedFrom":makeQuery(id+"F3.boolean.opBoolean","COPY",FACE,{"derivedFrom":makeQuery(id+"F3.opExtrude","CAP_FACE",FACE,{"disambiguationData":[OSD([subQ5,subQ1,subQ6,subQ7,subQ4,subQ3,subQ2,subQ0])],"isStart":false})})}),makeQuery(id+"F8.opExtrude","SWEPT_FACE",FACE,{"disambiguationData":[OSD([sQuery(id+"F7.wireOp",EDGE,"E67")])]})]});}
            var Q5;
            Q5=makeQuery(id+"F8.boolean.opBoolean","INTERSECT",EDGE,{"disambiguationData":[OD(0.0)],"derivedFrom":[makeQuery(id+"F5.opExtrude","SWEPT_FACE",FACE,{"disambiguationData":[OSD([sQuery(id+"F4.wireOp",EDGE,"E30")])]}),makeQuery(id+"F8.opExtrude","SWEPT_FACE",FACE,{"disambiguationData":[OSD([sQuery(id+"F7.wireOp",EDGE,"E67")])]})]});
            fillet(context, id + "F14", {"entities" : qUnion([Q0, Q1, Q2, Q3, Q4, Q5]), "radius" : 3 * mm, "tangentPropagation" : true, "allowEdgeOverflow" : false});
        }
        {
            var Q0;
            Q0=makeQuery(id+"F1.opExtrude","CAP_EDGE",EDGE,{"disambiguationData":[OSD([sQuery(id+"F0.wireOp",EDGE,"E1.bottom")])],"isStart":false});
            fillet(context, id + "F15", {"entities" : qUnion([Q0]), "radius" : 2 * mm, "tangentPropagation" : true, "allowEdgeOverflow" : false});
        }
        {
            var Q0;
            {var subQ0=sQuery(id+"F0.wireOp",EDGE,"E21.filletArc");var subQ1=sQuery(id+"F0.wireOp",EDGE,"E7");var subQ2=sQuery(id+"F0.wireOp",EDGE,"E6");var subQ3=sQuery(id+"F0.wireOp",EDGE,"E5");var subQ4=sQuery(id+"F0.wireOp",EDGE,"E4");var subQ5=sQuery(id+"F0.wireOp",EDGE,"E22.filletArc");var subQ6=sQuery(id+"F0.wireOp",EDGE,"E1.bottom");var subQ7=sQuery(id+"F0.wireOp",EDGE,"E1.right");var subQ8=sQuery(id+"F0.wireOp",EDGE,"E1.top");var subQ9=sQuery(id+"F0.wireOp",EDGE,"E1.left");var subQ10=sQuery(id+"F0.wireOp",EDGE,"E23.filletArc");var subQ11=sQuery(id+"F0.wireOp",EDGE,"E24.filletArc");Q0=makeQuery(id+"F2.boolean.opBoolean","SPLIT",FACE,{"disambiguationData":[TD([makeQuery(id+"F1.opExtrude","SWEPT_FACE",FACE,{"disambiguationData":[OSD([subQ6])]})])],"derivedFrom":makeQuery(id+"F1.opExtrude","CAP_FACE",FACE,{"disambiguationData":[OSD([subQ6,subQ8,subQ9,subQ7,subQ4,subQ3,subQ2,subQ1,subQ0,subQ5,subQ10,subQ11])],"isStart":true})});}
            var sketch = newSketch(context, id + "F16", { "sketchPlane" : qUnion([Q0])});
            skCircle(sketch, "E79", {"center": v(0, 120) * mm, "radius": 6 * mm});
            skArc(sketch, "E80", {"start": v(15, 120) * mm, "mid": v(0, 135) * mm, "end": v(-15, 120) * mm});
            skLineSegment(sketch, "E81", {"start": v(-15, 120) * mm, "end": v(-15, 108) * mm});
            skLineSegment(sketch, "E82", {"start": v(-15, 108) * mm, "end": v(-33, 90) * mm});
            skLineSegment(sketch, "E83", {"start": v(15, 120) * mm, "end": v(15, 108) * mm});
            skLineSegment(sketch, "E84", {"start": v(15, 108) * mm, "end": v(33, 90) * mm});
            skPoint(sketch, "E85.endSnap0", {"position": v(80, 0) * mm});
            skCircle(sketch, "E86.MirrorC", {"center": v(0, -120) * mm, "radius": 6 * mm});
            skArc(sketch, "E87.MirrorCS", {"start": v(15, -120) * mm, "mid": v(0, -135) * mm, "end": v(-15, -120) * mm});
            skLineSegment(sketch, "E88.MirrorCS", {"start": v(15, -120) * mm, "end": v(15, -108) * mm});
            skLineSegment(sketch, "E89.MirrorCS", {"start": v(-15, -120) * mm, "end": v(-15, -108) * mm});
            skLineSegment(sketch, "E90.MirrorCS", {"start": v(-15, -108) * mm, "end": v(-33, -90) * mm});
            skLineSegment(sketch, "E91.MirrorCS", {"start": v(15, -108) * mm, "end": v(33, -90) * mm});
            skPoint(sketch, "E92.orphan", {"position": v(-110.22, 0) * mm});
            skPoint(sketch, "E85.end.orphan", {"position": v(97.1, 0) * mm});
            skSolve(sketch);
        }
        {
            var Q0;
            Q0=makeQuery(id+"F16.imprint","IMPRINT",FACE,{"disambiguationData":[TD([[makeQuery(id+"F16.imprint","IMPRINT",EDGE,{"derivedFrom":sQuery(id+"F16.wireOp",EDGE,"E79")}),-1.0]])]});
            var Q1;
            Q1=makeQuery(id+"F16.imprint","IMPRINT",FACE,{"disambiguationData":[TD([[makeQuery(id+"F16.imprint","IMPRINT",EDGE,{"derivedFrom":makeQuery(id+"F1.opExtrude","CAP_EDGE",EDGE,{"disambiguationData":[OSD([sQuery(id+"F0.wireOp",EDGE,"E1.left")])],"isStart":true})}),-1.0]])]});
            var Q2;
            Q2=makeQuery(id+"F16.imprint","IMPRINT",FACE,{"disambiguationData":[TD([[makeQuery(id+"F16.imprint","IMPRINT",EDGE,{"derivedFrom":sQuery(id+"F16.wireOp",EDGE,"E86.MirrorC")}),1.0]])]});
            var Q3;
            Q3=makeQuery(id+"F2.opExtrude","CAP_FACE",FACE,{"disambiguationData":[OSD([sQuery(id+"F0.wireOp",EDGE,"E12"),sQuery(id+"F0.wireOp",EDGE,"E13"),sQuery(id+"F0.wireOp",EDGE,"E14"),sQuery(id+"F0.wireOp",EDGE,"E15"),sQuery(id+"F0.wireOp",EDGE,"E17.filletArc"),sQuery(id+"F0.wireOp",EDGE,"E18.filletArc"),sQuery(id+"F0.wireOp",EDGE,"E19.filletArc"),sQuery(id+"F0.wireOp",EDGE,"E20.filletArc"),sQuery(id+"F0.wireOp",EDGE,"E25.0"),sQuery(id+"F0.wireOp",EDGE,"E25.1"),sQuery(id+"F0.wireOp",EDGE,"E25.2"),sQuery(id+"F0.wireOp",EDGE,"E25.3"),sQuery(id+"F0.wireOp",EDGE,"E25.4"),sQuery(id+"F0.wireOp",EDGE,"E25.5"),sQuery(id+"F0.wireOp",EDGE,"E25.6"),sQuery(id+"F0.wireOp",EDGE,"E25.7")])],"isStart":false});
            extrude(context, id + "F17", {"entities" : qUnion([Q0, Q1, Q2]), "endBound" : BoundingType.UP_TO_SURFACE, "endBoundEntityFace" : qUnion([Q3]), "depth" : 25 * mm});
        }
    });
